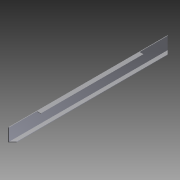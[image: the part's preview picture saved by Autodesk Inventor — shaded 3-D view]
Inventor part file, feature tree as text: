
AUTODESK INVENTOR PART (.ipt)
format: ipt  version: 2012 (Build 160160000, 160)  size: 98,816 bytes
history: native  units: in
note: dims shown in document units (in); Inventor stores cm internally (conversion verified against a paired STEP export)
features: extrude x3, sketch x2
ambient origin geometry x8: Origin, YZ Plane, XZ Plane, XY Plane, X Axis, Y Axis, Z Axis, Center Point
bodies: Solid1 (feature_tree)
feature tree (5):
  extrude  "Extrusion1"  Depth=1.0in
  sketch  "Sketch2"  dims[d2=0.125in d3=0.125in d4=0.125in d5=37.0in d6=0.0in d7=45.0deg d8=0.125in d9=6.5in d10=6.5in d11=28.0in d12=0.0in d13=28.0in d14=0.0in]
  extrude  "Extrusion2"  Depth=0.125in
  extrude  "Extrusion3"  Depth=0.125in
  sketch  "Sketch1"  dims[d0=3.0in d1=1.0in]
